# Revit family: Grohe_AngleValve_22074KF0
name_source: partatom
category: Plumbing Fixtures
units: mm (PartAtom-declared; Revit-internal decimal feet)

## family parameters
Cut with Voids When Loaded = No
Host = Face
OmniClass Number = 23.45.05.00
OmniClass Title = Sanitary Equipment
Part Type = Normal
Room Calculation Point = No
Round Connector Dimension = Use Diameter
Shared = No

## types (1)
- Angle Valve (22074KF0)
    Assembly Code = D2010
    AssetType = Fixed
    BIMObjectName = Grohe_AngleValve_22074KF0
    CO2NeutralProduction = GROHE is one of the first leading manufacturer within the sanitary industry having a CO2-neutral production.
    CW Connection = Yes
    ClassificationName = Uniclass2015
    ClassificationValue = Pr_65_54_95_06
    Color = Matt Black
    Cost = 0 $
    Default Elevation = 0 mm  [stored 0 ft]
    Description = Angle Valve
    DimensionsDocumentLink = https://cdn.cloud.grohe.com
    DocumentationCertificates = https://www.bimstore.co
    DocumentationInstallationGuide = https://www.bimstore.co
    DocumentationLiterature = https://www.bimstore.co
    DocumentationMaintenance = https://www.bimstore.co
    DocumentationTechnical = https://www.bimstore.co
    DurationUnit = Years
    EF000051 = Right-angled
    EF000113 = TRUE
    EF002147 = Handle
    EF002286 = External thread
    EF002671 = Black
    EF003454 = FALSE
    EF005464 = 0
    EF020781 = Top section, ceramic
    EF020785 = 1/2 inch
    EF020791 = Brass
    EF020963 = FALSE
    EF020969 = Compression ring
    EF020970 = 3/8 inch
    EF020971 = not relevant
    EF023662 = TRUE
    EF023686 = Other
    EFNL0001 = FALSE
    EFSE0002 = FALSE
    Ecojoy = No
    ExpectedLife = 0
    FullRecyclabilityOfPlastic = All plastic components are fully recyclable
    GROHESocialCommittment = green.grohe.com/social_engagement
    GROHESustainability = green.grohe.com
    HW Connection = Yes
    IfcExportAs = IfcPipeFitting
    IfcExportType = IfcPipeFittingType
    Keynote = N13
    Manufacturer = Grohe
    ManufacturerName = Grohe
    Model = Angle Valve
    ModelNumber = 22074KF0
    ModelReference = Angle Valve
    NBSDescription = Ball valves
    NBSObjectName = Grohe - Ball valves
    NBSReference = 90-10-90/330
    NominalDepth = 0 mm  [stored 0 ft]
    NominalHeight = 0 mm  [stored 0 ft]
    NominalLength = 0 mm  [stored 0 ft]
    PrimaryMaterial = Grohe_MattBlack
    ProductDescription = pre-roughened connection thread for easy sealing

wall connection 1/2"

outlet 3/8"

with length compensation

with compression nut Ø 10 mm

water protected spindle shutoff, brass,

with grease chamber and double o-ring sealing

long connecting shaft

ergonomic metal handle

marking: neutral

metal push-on escutcheon Ø 55 mm

GROHE Long-Life Shine finish
    ProductNumber = 22074KF0
    ProductPageURL = https://www.grohe.co.uk
    ProductShortText = Angle Valves Angle valve 1/2"
    ProductType = Classic Tap and Valve
    ProductionYear = 2023
    SustainabilityAward = green.grohe.com/awards
    SustainabilityReport = green.grohe.com/reporting
    Type Comments = Angle Valve
    TypeName = Angle Valve
    URL = https://www.grohe.co.uk
    Vent Connection = No
    WarrantyDurationLabor = 0
    WarrantyDurationParts = 0
    WarrantyDurationUnit = Years
    Waste Connection = No
    _BSBibleVersion = 17
    _BimSpecGuid = 0
    _CurrentRevision = 1
    _DistributedBy = https://www.bimstore.co
    _ObjectUserGuide = https://www.bimstore.co

note: [stored X ft] marks values corroborated as IEEE doubles in the binary element streams (Revit-internal decimal feet)

## geometry (parser evidence)
native form markers: Sweep x2
no freeform markers — native parametric forms only
